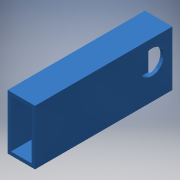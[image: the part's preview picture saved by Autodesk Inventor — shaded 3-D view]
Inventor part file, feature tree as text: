
AUTODESK INVENTOR PART (.ipt)
format: ipt  version: 2017 SP1 (Build 210196100, 196)  size: 114,176 bytes
history: native  units: in
note: dims shown in document units (in); Inventor stores cm internally (conversion verified against a paired STEP export)
features: extrude x2, sketch x2
ambient origin geometry x8: Origin, YZ Plane, XZ Plane, XY Plane, X Axis, Y Axis, Z Axis, Center Point
bodies: Solid1 (feature_tree)
feature tree (4):
  extrude  "Extrusion1"  Depth=1.0in
  extrude  "Extrusion2"  Depth=0.125in
  sketch  "Sketch1"  dims[d0=2.0in d1=1.0in]
  sketch  "Sketch2"  dims[d2=0.125in d3=0.125in d4=5.0in d5=0.0in d6=0.875in d7=0.75in d8=0.75in d9=6.0in d10=0.0in]
